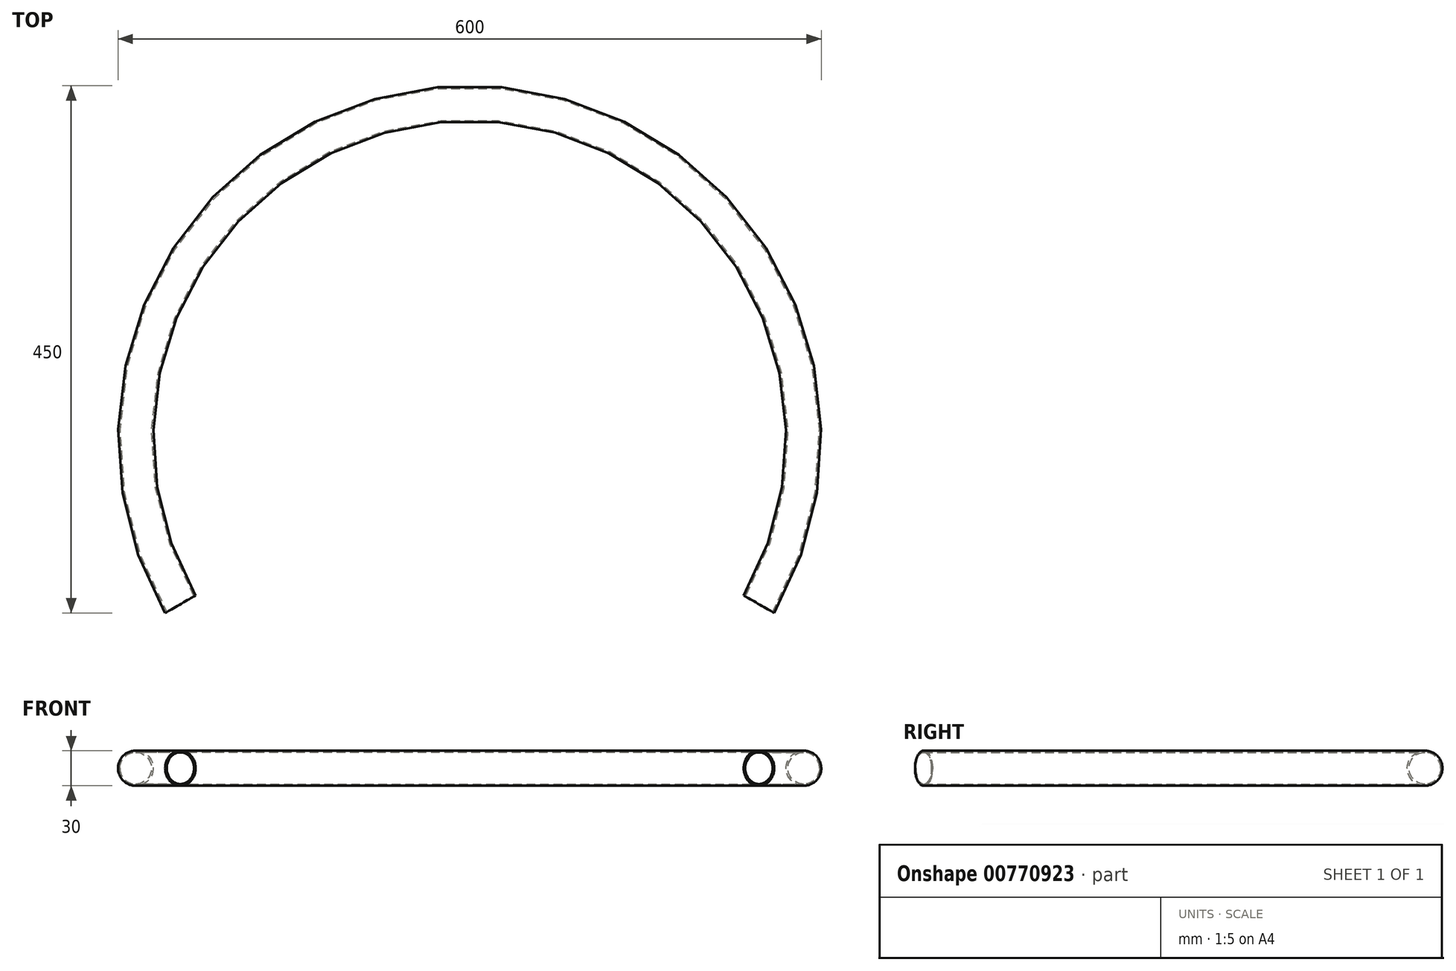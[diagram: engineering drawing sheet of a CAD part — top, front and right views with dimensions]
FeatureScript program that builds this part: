
annotation { "Feature Type Name" : "Feature", "Feature Type Description" : "" }
export const myFeature = defineFeature(function(context is Context, id is Id, definition is map)
    precondition{}
    {
        {
            var Q0;
            Q0=qCreatedBy(makeId("Top.planeOp"),FACE);
            var sketch = newSketch(context, id + "F0", { "sketchPlane" : qUnion([Q0])});
            skCircle(sketch, "E0", {"center": v(0, 0) * mm, "radius": 300 * mm});
            skCircle(sketch, "E1.0", {"center": v(0, 0) * mm, "radius": 270 * mm});
            skCircle(sketch, "E2.0", {"center": v(0, 0) * mm, "radius": 285 * mm});
            skSolve(sketch);
        }
        {
            var Q0;
            Q0=qCreatedBy(makeId("Front.planeOp"),FACE);
            var sketch = newSketch(context, id + "F1", { "sketchPlane" : qUnion([Q0])});
            skCircle(sketch, "E3", {"center": v(-285, 0) * mm, "radius": 15 * mm});
            skCircle(sketch, "E4", {"center": v(-285, 0) * mm, "radius": 13.5 * mm});
            skSolve(sketch);
        }
        {
            var Q0;
            Q0=makeQuery(id+"F1.imprint","IMPRINT",FACE,{"disambiguationData":[TD([[makeQuery(id+"F1.imprint","IMPRINT",EDGE,{"derivedFrom":sQuery(id+"F1.wireOp",EDGE,"E3")}),1.0]])]});
            var Q1;
            Q1=sQuery(id+"F0.wireOp",EDGE,"E2.0");
            sweep(context, id + "F2", {"profiles" : qUnion([Q0]), "path" : qUnion([Q1])});
        }
        {
            var Q0;
            Q0=qCreatedBy(makeId("Top.planeOp"),FACE);
            var sketch = newSketch(context, id + "F3", { "sketchPlane" : qUnion([Q0])});
            skLineSegment(sketch, "E5", {"start": v(0, 0) * mm, "end": v(-793.94, -458.38) * mm});
            skLineSegment(sketch, "E6", {"start": v(-793.94, -458.38) * mm, "end": v(793.94, -458.38) * mm});
            skLineSegment(sketch, "E7", {"start": v(793.94, -458.38) * mm, "end": v(0, 0) * mm});
            skLineSegment(sketch, "E8", {"start": v(0, 0) * mm, "end": v(0, -365.05) * mm});
            skSolve(sketch);
        }
        {
            var Q0;
            Q0 = qSketchRegion(id + "F3", true);
            extrude(context, id + "F4", {"entities" : qUnion([Q0]), "operationType" : NewBodyOperationType.REMOVE, "endBound" : BoundingType.THROUGH_ALL, "depth" : 25 * mm, "offsetDistance" : 25 * mm, "hasSecondDirection" : true, "secondDirectionBound" : SecondDirectionBoundingType.THROUGH_ALL, "secondDirectionOppositeDirection" : true, "secondDirectionDepth" : 25 * mm});
        }
    });
